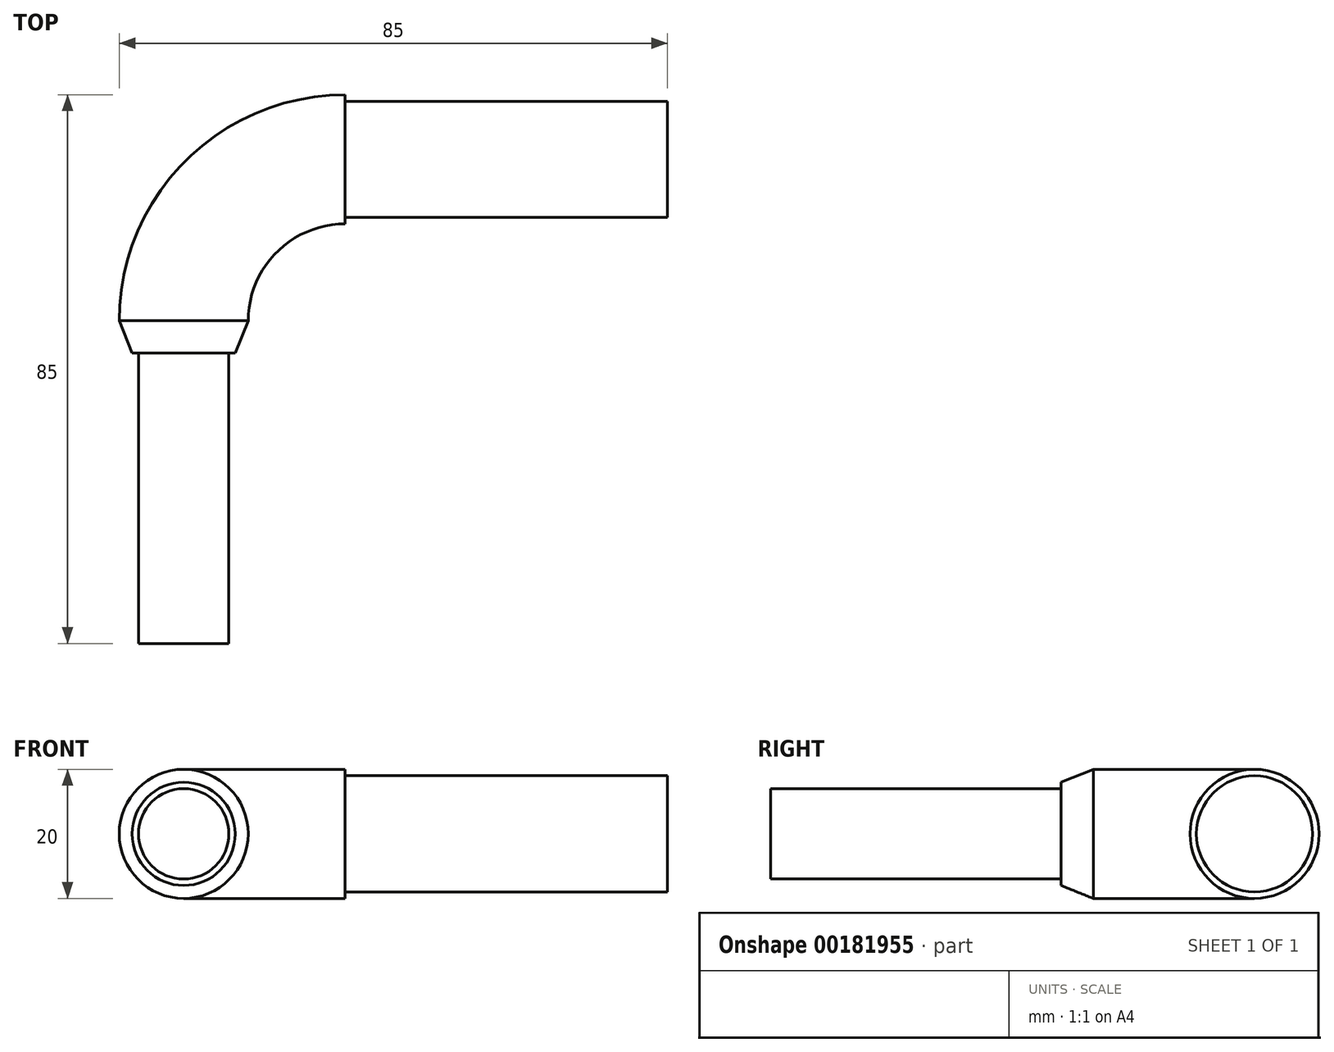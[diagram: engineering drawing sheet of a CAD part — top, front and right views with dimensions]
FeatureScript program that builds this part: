
annotation { "Feature Type Name" : "Feature", "Feature Type Description" : "" }
export const myFeature = defineFeature(function(context is Context, id is Id, definition is map)
    precondition{}
    {
        {
            var Q0;
            Q0=qCreatedBy(makeId("Front.planeOp"),FACE);
            var sketch = newSketch(context, id + "F0", { "sketchPlane" : qUnion([Q0])});
            skCircle(sketch, "E0", {"center": v(-40.36, 0) * mm, "radius": 10 * mm});
            skSolve(sketch);
        }
        {
            var Q0;
            Q0=qCreatedBy(makeId("Top.planeOp"),FACE);
            var sketch = newSketch(context, id + "F1", { "sketchPlane" : qUnion([Q0])});
            skArc(sketch, "E1", {"start": v(-40.36, 0) * mm, "mid": v(-33.04, 17.68) * mm, "end": v(-15.36, 25) * mm, "construction": true});
            skLineSegment(sketch, "E2", {"start": v(-15.36, 0) * mm, "end": v(-15.36, 25) * mm, "construction": true});
            skLineSegment(sketch, "E3", {"start": v(-40.36, 0) * mm, "end": v(-15.36, 0) * mm, "construction": true});
            skSolve(sketch);
        }
        {
            var Q0;
            Q0=qCreatedBy(makeId("Front.planeOp"),FACE);
            var sketch = newSketch(context, id + "F2", { "sketchPlane" : qUnion([Q0])});
            skLineSegment(sketch, "E4", {"start": v(-15.36, -11.93) * mm, "end": v(-15.36, 24.76) * mm, "construction": true});
            skSolve(sketch);
        }
        {
            var Q0;
            Q0=makeQuery(id+"F0.imprint","IMPRINT",FACE,{"disambiguationData":[TD([[makeQuery(id+"F0.imprint","IMPRINT",EDGE,{"derivedFrom":sQuery(id+"F0.wireOp",EDGE,"E0")}),1.0]])]});
            var Q1;
            Q1=sQuery(id+"F2.wireOp",EDGE,"E4");
            revolve(context, id + "F3", {"entities" : qUnion([Q0]), "axis" : qUnion([Q1]), "revolveType" : RevolveType.ONE_DIRECTION, "oppositeDirection" : true, "angle" : 90 * degree});
        }
        {
            var Q0;
            Q0=makeQuery(id+"F3.opRevolve","CAP_FACE",FACE,{"disambiguationData":[OSD([sQuery(id+"F0.wireOp",EDGE,"E0")])],"isStart":true});
            var sketch = newSketch(context, id + "F4", { "sketchPlane" : qUnion([Q0])});
            skCircle(sketch, "E5", {"center": v(-40.36, 0) * mm, "radius": 7 * mm});
            skSolve(sketch);
        }
        {
            var Q0;
            Q0=makeQuery(id+"F4.imprint","IMPRINT",FACE,{"disambiguationData":[TD([[makeQuery(id+"F4.imprint","IMPRINT",EDGE,{"derivedFrom":sQuery(id+"F4.wireOp",EDGE,"E5")}),1.0]])]});
            var Q1;
            Q1=sQuery(id+"F4.wireOp",EDGE,"E5");
            extrude(context, id + "F5", {"entities" : qUnion([Q0]), "surfaceEntities" : qUnion([Q1]), "depth" : 50 * mm});
        }
        {
            var Q0;
            Q0=makeQuery(id+"F3.opRevolve","CAP_FACE",FACE,{"disambiguationData":[OSD([sQuery(id+"F0.wireOp",EDGE,"E0")])],"isStart":false});
            var sketch = newSketch(context, id + "F6", { "sketchPlane" : qUnion([Q0])});
            skCircle(sketch, "E6", {"center": v(25, 0) * mm, "radius": 9 * mm});
            skSolve(sketch);
        }
        {
            var Q0;
            Q0=makeQuery(id+"F6.imprint","IMPRINT",FACE,{"disambiguationData":[TD([[makeQuery(id+"F6.imprint","IMPRINT",EDGE,{"derivedFrom":sQuery(id+"F6.wireOp",EDGE,"E6")}),1.0]])]});
            extrude(context, id + "F7", {"entities" : qUnion([Q0]), "operationType" : NewBodyOperationType.ADD, "depth" : 50 * mm});
        }
        {
            var Q0;
            Q0=makeQuery(id+"F3.opRevolve","CAP_FACE",FACE,{"disambiguationData":[OSD([sQuery(id+"F0.wireOp",EDGE,"E0")])],"isStart":true});
            extrude(context, id + "F8", {"entities" : qUnion([Q0]), "operationType" : NewBodyOperationType.ADD, "depth" : 5 * mm});
        }
        {
            var Q0;
            Q0=makeQuery(id+"F8.opExtrude","CAP_EDGE",EDGE,{"disambiguationData":[OSD([sQuery(id+"F0.wireOp",EDGE,"E0")])],"isStart":false});
            chamfer(context, id + "F9", {"entities" : qUnion([Q0]), "chamferType" : ChamferType.TWO_OFFSETS, "width1" : 2 * mm, "oppositeDirection" : false, "width2" : 5 * mm, "tangentPropagation" : true});
        }
    });
